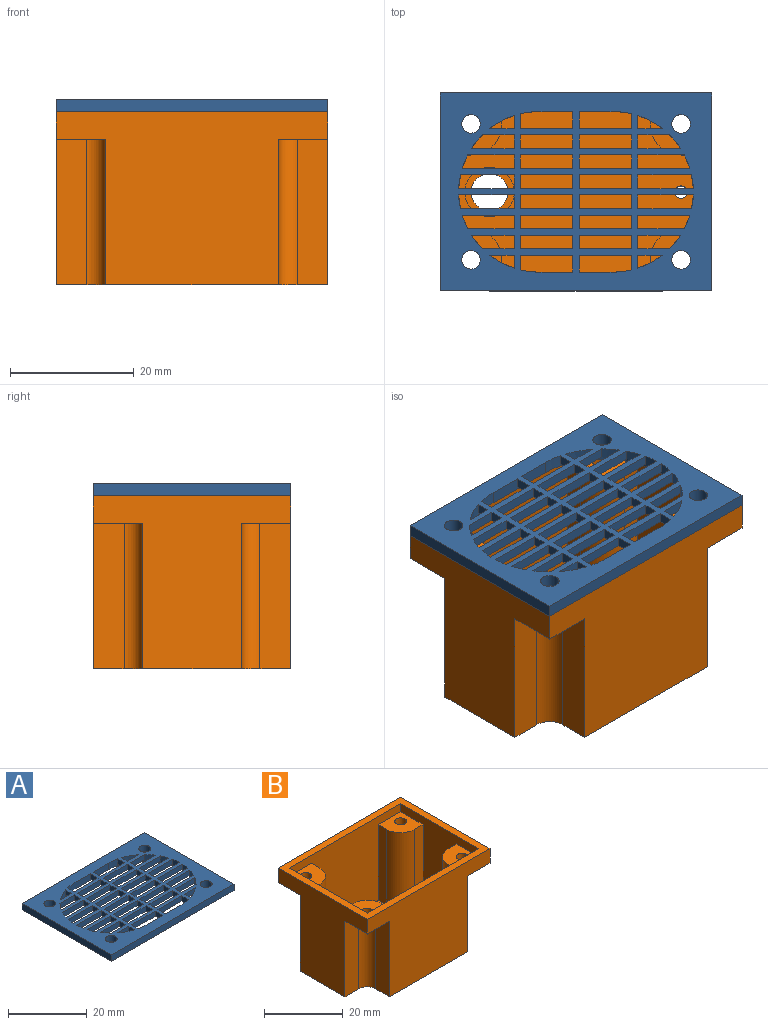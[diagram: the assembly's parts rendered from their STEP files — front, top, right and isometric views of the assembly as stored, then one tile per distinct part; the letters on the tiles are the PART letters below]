
ASSEMBLY  parts=2 mates=1
PART A: 119 faces, bbox 44x32x2 mm
  f0: plane 44x2mm, normal (0,1,0), area 88mm2, adj f1,f11,f12,f117
  f1: plane 32x2mm, normal (-1,0,0), area 64mm2, adj f0,f2,f12,f117
  f2: plane 44x2mm, normal (0,-1,0), area 88mm2, adj f1,f11,f12,f117
  f3: cylinder r=13mm len=26mm, axis (0,0,-1), area 64.9mm2, adj f4,f10,f12,f49,f60,f61,f63,f65
  f4: plane 12x2mm, normal (0,1,0), area 22.4mm2, adj f3,f5,f12,f50,f58,f117,f118
  f5: cylinder r=13mm len=26mm, axis (0,0,-1), area 64.9mm2, adj f4,f10,f12,f51,f52,f53,f54,f55
  f6: cylinder r=1.5mm len=3mm, axis (0,0,-1), area 18.8mm2, adj f12,f117
  f7: cylinder r=1.5mm len=3mm, axis (0,0,-1), area 18.8mm2, adj f12,f117
  f8: cylinder r=1.5mm len=3mm, axis (0,0,-1), area 18.8mm2, adj f12,f117
  f9: cylinder r=1.5mm len=3mm, axis (0,0,-1), area 18.8mm2, adj f12,f117
  f10: plane 12x2mm, normal (0,-1,0), area 22.4mm2, adj f3,f5,f12,f76,f78,f117,f118
  f11: plane 32x2mm, normal (1,0,0), area 64mm2, adj f0,f2,f12,f117
  f12: plane 44x32mm, normal (0,0,-1), area 536.8mm2, adj f0,f1,f2,f3,f4,f5,f6,f7
  f13: plane 8.5x1.6mm, normal (0,-1,0), area 13.6mm2, adj f14,f116,f117,f118
  f14: plane 2.25x1.6mm, normal (-1,0,0), area 3.6mm2, adj f13,f15,f117,f118
  f15: plane 8.5x1.6mm, normal (0,1,0), area 13.6mm2, adj f14,f116,f117,f118
  f16: plane 8.5x1.6mm, normal (0,-1,0), area 13.6mm2, adj f17,f86,f117,f118
  f17: plane 2.25x1.6mm, normal (-1,0,0), area 3.6mm2, adj f16,f18,f117,f118
  f18: plane 8.5x1.6mm, normal (0,1,0), area 13.6mm2, adj f17,f86,f117,f118
  f19: plane 8.5x1.6mm, normal (0,-1,0), area 13.6mm2, adj f20,f87,f117,f118
  f20: plane 2.25x1.6mm, normal (-1,0,0), area 3.6mm2, adj f19,f21,f117,f118
  f21: plane 8.5x1.6mm, normal (0,1,0), area 13.6mm2, adj f20,f87,f117,f118
  f22: plane 8.5x1.6mm, normal (0,-1,0), area 13.6mm2, adj f23,f88,f117,f118
  f23: plane 2.25x1.6mm, normal (-1,0,0), area 3.6mm2, adj f22,f24,f117,f118
  f24: plane 8.5x1.6mm, normal (0,1,0), area 13.6mm2, adj f23,f88,f117,f118
  f25: plane 8.5x1.6mm, normal (0,-1,0), area 13.6mm2, adj f26,f89,f117,f118
  f26: plane 2.25x1.6mm, normal (-1,0,0), area 3.6mm2, adj f25,f27,f117,f118
  f27: plane 8.5x1.6mm, normal (0,1,0), area 13.6mm2, adj f26,f89,f117,f118
  f28: plane 8.5x1.6mm, normal (0,-1,0), area 13.6mm2, adj f29,f90,f117,f118
  f29: plane 2.25x1.6mm, normal (-1,0,0), area 3.6mm2, adj f28,f30,f117,f118
  f30: plane 8.5x1.6mm, normal (0,1,0), area 13.6mm2, adj f29,f90,f117,f118
  f31: plane 2.25x1.6mm, normal (-1,0,0), area 3.6mm2, adj f32,f91,f117,f118
  f32: plane 8.5x1.6mm, normal (0,1,0), area 13.6mm2, adj f31,f33,f117,f118
  f33: plane 2.25x1.6mm, normal (1,0,0), area 3.6mm2, adj f32,f91,f117,f118
  f34: plane 2.25x1.6mm, normal (-1,0,0), area 3.6mm2, adj f35,f92,f117,f118
  f35: plane 8.5x1.6mm, normal (0,1,0), area 13.6mm2, adj f34,f36,f117,f118
  f36: plane 2.25x1.6mm, normal (1,0,0), area 3.6mm2, adj f35,f92,f117,f118
  f37: plane 2.25x1.6mm, normal (-1,0,0), area 3.6mm2, adj f38,f93,f117,f118
  f38: plane 8.5x1.6mm, normal (0,1,0), area 13.6mm2, adj f37,f39,f117,f118
  f39: plane 2.25x1.6mm, normal (1,0,0), area 3.6mm2, adj f38,f93,f117,f118
  f40: plane 2.25x1.6mm, normal (-1,0,0), area 3.6mm2, adj f41,f94,f117,f118
  f41: plane 8.5x1.6mm, normal (0,1,0), area 13.6mm2, adj f40,f42,f117,f118
  f42: plane 2.25x1.6mm, normal (1,0,0), area 3.6mm2, adj f41,f94,f117,f118
  f43: plane 2.25x1.6mm, normal (-1,0,0), area 3.6mm2, adj f44,f95,f117,f118
  f44: plane 8.5x1.6mm, normal (0,1,0), area 13.6mm2, adj f43,f45,f117,f118
  f45: plane 2.25x1.6mm, normal (1,0,0), area 3.6mm2, adj f44,f95,f117,f118
  f46: plane 2.25x1.6mm, normal (-1,0,0), area 3.6mm2, adj f47,f96,f117,f118
  f47: plane 8.5x1.6mm, normal (0,1,0), area 13.6mm2, adj f46,f48,f117,f118
  f48: plane 2.25x1.6mm, normal (1,0,0), area 3.6mm2, adj f47,f96,f117,f118
  f49: plane 2.4x1.6mm, normal (-1,0,0), area 3.8mm2, adj f3,f97,f117,f118
  f50: plane 2.75x1.6mm, normal (1,0,0), area 4.4mm2, adj f4,f97,f117,f118
  f51: plane 8.71x1.6mm, normal (0,1,0), area 13.9mm2, adj f5,f98,f117,f118
  f52: plane 8.99x1.6mm, normal (0,-1,0), area 14.4mm2, adj f5,f98,f117,f118
  f53: plane 7.53x1.6mm, normal (0,1,0), area 12.1mm2, adj f5,f99,f117,f118
  f54: plane 8.45x1.6mm, normal (0,-1,0), area 13.5mm2, adj f5,f99,f117,f118
  f55: plane 5.13x1.6mm, normal (0,1,0), area 8.2mm2, adj f5,f100,f117,f118
  f56: plane 6.95x1.6mm, normal (0,-1,0), area 11.1mm2, adj f5,f100,f117,f118
  f57: plane 2.12x1.6mm, normal (-1,0,0), area 3.4mm2, adj f5,f101,f117,f118
  f58: plane 2.75x1.6mm, normal (-1,0,0), area 4.4mm2, adj f4,f102,f117,f118
  f59: plane 2.4x1.6mm, normal (1,0,0), area 3.8mm2, adj f5,f102,f117,f118
  f60: plane 4x1.6mm, normal (0,-1,0), area 6.4mm2, adj f3,f103,f117,f118
  f61: plane 5.13x1.6mm, normal (0,1,0), area 8.2mm2, adj f3,f62,f117,f118
  f62: plane 2.25x1.6mm, normal (1,0,0), area 3.6mm2, adj f61,f104,f117,f118
  f63: plane 7.53x1.6mm, normal (0,1,0), area 12.1mm2, adj f3,f64,f117,f118
  f64: plane 2.25x1.6mm, normal (1,0,0), area 3.6mm2, adj f63,f105,f117,f118
  f65: plane 8.71x1.6mm, normal (0,1,0), area 13.9mm2, adj f3,f66,f117,f118
  f66: plane 2.25x1.6mm, normal (1,0,0), area 3.6mm2, adj f65,f106,f117,f118
  f67: plane 8.99x1.6mm, normal (0,1,0), area 14.4mm2, adj f3,f68,f117,f118
  f68: plane 2.25x1.6mm, normal (1,0,0), area 3.6mm2, adj f67,f107,f117,f118
  f69: plane 8.45x1.6mm, normal (0,1,0), area 13.5mm2, adj f3,f70,f117,f118
  f70: plane 2.25x1.6mm, normal (1,0,0), area 3.6mm2, adj f69,f108,f117,f118
  f71: plane 6.95x1.6mm, normal (0,1,0), area 11.1mm2, adj f3,f72,f117,f118
  f72: plane 2.25x1.6mm, normal (1,0,0), area 3.6mm2, adj f71,f109,f117,f118
  f73: plane 4x1.6mm, normal (0,1,0), area 6.4mm2, adj f3,f110,f117,f118
  f74: plane 2.4x1.6mm, normal (-1,0,0), area 3.8mm2, adj f3,f75,f117,f118
  f75: plane 8.5x1.6mm, normal (0,1,0), area 13.6mm2, adj f74,f76,f117,f118
  f76: plane 2.75x1.6mm, normal (1,0,0), area 4.4mm2, adj f10,f75,f117,f118
  f77: plane 2.4x1.6mm, normal (1,0,0), area 3.8mm2, adj f5,f111,f117,f118
  f78: plane 2.75x1.6mm, normal (-1,0,0), area 4.4mm2, adj f10,f111,f117,f118
  f79: plane 4x1.6mm, normal (0,1,0), area 6.4mm2, adj f5,f112,f117,f118
  f80: plane 8.71x1.6mm, normal (0,-1,0), area 13.9mm2, adj f5,f81,f117,f118
  f81: plane 2.25x1.6mm, normal (-1,0,0), area 3.6mm2, adj f80,f113,f117,f118
  f82: plane 6.95x1.6mm, normal (0,1,0), area 11.1mm2, adj f5,f114,f117,f118
  f83: plane 5.13x1.6mm, normal (0,-1,0), area 8.2mm2, adj f5,f114,f117,f118
  f84: plane 8.45x1.6mm, normal (0,1,0), area 13.5mm2, adj f5,f115,f117,f118
  f85: plane 7.53x1.6mm, normal (0,-1,0), area 12.1mm2, adj f5,f115,f117,f118
  f86: plane 2.25x1.6mm, normal (1,0,0), area 3.6mm2, adj f16,f18,f117,f118
  f87: plane 2.25x1.6mm, normal (1,0,0), area 3.6mm2, adj f19,f21,f117,f118
  f88: plane 2.25x1.6mm, normal (1,0,0), area 3.6mm2, adj f22,f24,f117,f118
  f89: plane 2.25x1.6mm, normal (1,0,0), area 3.6mm2, adj f25,f27,f117,f118
  f90: plane 2.25x1.6mm, normal (1,0,0), area 3.6mm2, adj f28,f30,f117,f118
  f91: plane 8.5x1.6mm, normal (0,-1,0), area 13.6mm2, adj f31,f33,f117,f118
  f92: plane 8.5x1.6mm, normal (0,-1,0), area 13.6mm2, adj f34,f36,f117,f118
  f93: plane 8.5x1.6mm, normal (0,-1,0), area 13.6mm2, adj f37,f39,f117,f118
  f94: plane 8.5x1.6mm, normal (0,-1,0), area 13.6mm2, adj f40,f42,f117,f118
  f95: plane 8.5x1.6mm, normal (0,-1,0), area 13.6mm2, adj f43,f45,f117,f118
  f96: plane 8.5x1.6mm, normal (0,-1,0), area 13.6mm2, adj f46,f48,f117,f118
  f97: plane 8.5x1.6mm, normal (0,-1,0), area 13.6mm2, adj f49,f50,f117,f118
  f98: plane 2.25x1.6mm, normal (-1,0,0), area 3.6mm2, adj f51,f52,f117,f118
  f99: plane 2.25x1.6mm, normal (-1,0,0), area 3.6mm2, adj f53,f54,f117,f118
  f100: plane 2.25x1.6mm, normal (-1,0,0), area 3.6mm2, adj f55,f56,f117,f118
  f101: plane 4x1.6mm, normal (0,-1,0), area 6.4mm2, adj f5,f57,f117,f118
  f102: plane 8.5x1.6mm, normal (0,-1,0), area 13.6mm2, adj f58,f59,f117,f118
  f103: plane 2.12x1.6mm, normal (1,0,0), area 3.4mm2, adj f3,f60,f117,f118
  f104: plane 6.95x1.6mm, normal (0,-1,0), area 11.1mm2, adj f3,f62,f117,f118
  f105: plane 8.45x1.6mm, normal (0,-1,0), area 13.5mm2, adj f3,f64,f117,f118
  f106: plane 8.99x1.6mm, normal (0,-1,0), area 14.4mm2, adj f3,f66,f117,f118
  f107: plane 8.71x1.6mm, normal (0,-1,0), area 13.9mm2, adj f3,f68,f117,f118
  f108: plane 7.53x1.6mm, normal (0,-1,0), area 12.1mm2, adj f3,f70,f117,f118
  f109: plane 5.13x1.6mm, normal (0,-1,0), area 8.2mm2, adj f3,f72,f117,f118
  f110: plane 2.12x1.6mm, normal (1,0,0), area 3.4mm2, adj f3,f73,f117,f118
  f111: plane 8.5x1.6mm, normal (0,1,0), area 13.6mm2, adj f77,f78,f117,f118
  f112: plane 2.12x1.6mm, normal (-1,0,0), area 3.4mm2, adj f5,f79,f117,f118
  f113: plane 8.99x1.6mm, normal (0,1,0), area 14.4mm2, adj f5,f81,f117,f118
  f114: plane 2.25x1.6mm, normal (-1,0,0), area 3.6mm2, adj f82,f83,f117,f118
  f115: plane 2.25x1.6mm, normal (-1,0,0), area 3.6mm2, adj f84,f85,f117,f118
  f116: plane 2.25x1.6mm, normal (1,0,0), area 3.6mm2, adj f13,f15,f117,f118
  f117: plane 44x32mm, normal (0,0,1), area 831.6mm2, adj f0,f1,f2,f3,f4,f5,f6,f7
  f118: plane 38x26mm, normal (0,0,-1), area 294.8mm2, adj f3,f4,f5,f10,f13,f14,f15,f16
PART B: 51 faces, bbox 44x32x28 mm
  f0: plane 8x8mm, normal (0,0,1), area 51.6mm2, adj f25,f37,f38,f39,f40,f44
  f1: plane 8x8mm, normal (0,0,1), area 51.6mm2, adj f25,f26,f27,f28,f29,f47
  f2: plane 8x8mm, normal (0,0,1), area 51.6mm2, adj f33,f34,f35,f36,f37,f45
  f3: plane 23.5x5mm, normal (0,-1,0), area 117.5mm2, adj f4,f20,f22,f41
  f4: cylinder r=3mm len=23.5mm, axis (0,0,-1), area 110.7mm2, adj f3,f5,f22,f41
  f5: plane 23.5x5mm, normal (-1,0,0), area 117.5mm2, adj f4,f6,f22,f41
  f6: plane 44x28mm, normal (0,-1,0), area 856mm2, adj f5,f7,f10,f20,f22,f41,f42,f50
  f7: plane 23.5x5mm, normal (1,0,0), area 117.5mm2, adj f6,f8,f22,f42
  f8: cylinder r=3mm len=23.5mm, axis (0,0,-1), area 110.7mm2, adj f7,f9,f22,f42
  f9: plane 23.5x5mm, normal (0,-1,0), area 117.5mm2, adj f8,f10,f22,f42
  f10: plane 32x28mm, normal (1,0,0), area 520mm2, adj f6,f9,f11,f14,f22,f42,f43,f50
  f11: plane 23.5x5mm, normal (0,1,0), area 117.5mm2, adj f10,f12,f22,f43
  f12: cylinder r=3mm len=23.5mm, axis (0,0,-1), area 110.7mm2, adj f11,f13,f22,f43
  f13: plane 23.5x5mm, normal (1,0,0), area 117.5mm2, adj f12,f14,f22,f43
  f14: plane 44x28mm, normal (0,1,0), area 856mm2, adj f10,f13,f15,f20,f22,f43,f49,f50
  f15: plane 23.5x5mm, normal (-1,0,0), area 117.5mm2, adj f14,f16,f22,f49
  f16: cylinder r=3mm len=23.5mm, axis (0,0,-1), area 110.7mm2, adj f15,f17,f22,f49
  f17: plane 23.5x5mm, normal (0,1,0), area 117.5mm2, adj f16,f20,f22,f49
  f18: cylinder r=1mm len=2mm, axis (0,0,-1), area 12.6mm2, adj f21,f22
  f19: cylinder r=3mm len=8mm, axis (0,0,-1), area 150.8mm2, adj f22,f24
  f20: plane 32x28mm, normal (-1,0,0), area 520mm2, adj f3,f6,f14,f17,f22,f41,f49,f50
  f21: plane 40x28mm, normal (0,0,1), area 832.1mm2, adj f18,f23,f25,f26,f27,f28,f29,f30
  f22: plane 44x32mm, normal (0,0,-1), area 1128.3mm2, adj f3,f4,f5,f6,f7,f8,f9,f10
  f23: cylinder r=4mm len=8mm, axis (0,0,-1), area 150.8mm2, adj f21,f24
  f24: plane 8x8mm, normal (0,0,1), area 22mm2, adj f19,f23
  f25: plane 40x26mm, normal (0,1,0), area 664mm2, adj f0,f1,f21,f26,f29,f37,f40,f50
  f26: plane 23.5x3mm, normal (1,0,0), area 70.5mm2, adj f1,f21,f25,f27
  f27: cylinder r=5mm len=23.5mm, axis (0,0,-1), area 184.6mm2, adj f1,f21,f26,f28
  f28: plane 23.5x3mm, normal (0,1,0), area 70.5mm2, adj f1,f21,f27,f29
  f29: plane 28x26mm, normal (1,0,0), area 352mm2, adj f1,f21,f25,f28,f30,f33,f48,f50
  f30: plane 23.5x3mm, normal (0,-1,0), area 70.5mm2, adj f21,f29,f31,f48
  f31: cylinder r=5mm len=23.5mm, axis (0,0,-1), area 184.6mm2, adj f21,f30,f32,f48
  f32: plane 23.5x3mm, normal (1,0,0), area 70.5mm2, adj f21,f31,f33,f48
  f33: plane 40x26mm, normal (0,-1,0), area 664mm2, adj f2,f21,f29,f32,f34,f37,f48,f50
  f34: plane 23.5x3mm, normal (-1,0,0), area 70.5mm2, adj f2,f21,f33,f35
  f35: cylinder r=5mm len=23.5mm, axis (0,0,-1), area 184.6mm2, adj f2,f21,f34,f36
  f36: plane 23.5x3mm, normal (0,-1,0), area 70.5mm2, adj f2,f21,f35,f37
  f37: plane 28x26mm, normal (-1,0,0), area 352mm2, adj f0,f2,f21,f25,f33,f36,f38,f50
  f38: plane 23.5x3mm, normal (0,1,0), area 70.5mm2, adj f0,f21,f37,f39
  f39: cylinder r=5mm len=23.5mm, axis (0,0,-1), area 184.6mm2, adj f0,f21,f38,f40
  f40: plane 23.5x3mm, normal (-1,0,0), area 70.5mm2, adj f0,f21,f25,f39
  f41: plane 8x8mm, normal (0,0,-1), area 55mm2, adj f3,f4,f5,f6,f20,f47
  f42: plane 8x8mm, normal (0,0,-1), area 55mm2, adj f6,f7,f8,f9,f10,f44
  f43: plane 8x8mm, normal (0,0,-1), area 55mm2, adj f10,f11,f12,f13,f14,f45
  f44: cylinder r=1.5mm len=3mm, axis (0,0,-1), area 18.8mm2, adj f0,f42
  f45: cylinder r=1.5mm len=3mm, axis (0,0,-1), area 18.8mm2, adj f2,f43
  f46: cylinder r=1.5mm len=3mm, axis (0,0,-1), area 18.8mm2, adj f48,f49
  f47: cylinder r=1.5mm len=3mm, axis (0,0,-1), area 18.8mm2, adj f1,f41
  f48: plane 8x8mm, normal (0,0,1), area 51.6mm2, adj f29,f30,f31,f32,f33,f46
  f49: plane 8x8mm, normal (0,0,-1), area 55mm2, adj f14,f15,f16,f17,f20,f46
  f50: plane 44x32mm, normal (0,0,1), area 288mm2, adj f6,f10,f14,f20,f25,f29,f33,f37
PLACE A t=(-36.37,66.6,20.24)mm
PLACE B t=(-36.37,32.6,-7.76)mm
MATE fastened A.f12 <-> B.f50  axis (0,0,1) through (7.63,30.6,20.24)mm
